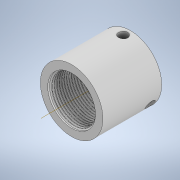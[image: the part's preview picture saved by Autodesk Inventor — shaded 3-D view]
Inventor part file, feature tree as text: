
AUTODESK INVENTOR PART (.ipt)
format: ipt  version: 2021.1 (Build 251245000, 245)  size: 671,232 bytes
history: native  units: in
note: dims shown in document units (in); Inventor stores cm internally (conversion verified against a paired STEP export)
features: sketch x4, extrude x2, helix x1, plane x1, hole x1, pattern_circular x1
ambient origin geometry x8: Origin, YZ Plane, XZ Plane, XY Plane, X Axis, Y Axis, Z Axis, Center Point
bodies: Body1 (feature_tree)
feature tree (10):
  extrude  "Extrusion3"  Depth=2.125in
  extrude  "Extrusion4"  Depth=1.6232in
  helix  "Coil2"  [1 undecoded]
  plane  "Work Plane1"
  hole  "Hole1"  [1 undecoded]
  pattern_circular  "Circular Pattern1"  [2 undecoded]
  sketch  "Sketch3"  dims[d8=0.635in d9=2.125in]
  sketch  "Sketch4"  dims[d10=2.0in d11=0.0in d12=1.6232in d13=1.5in]
  sketch  "Sketch5"  dims[d14=0.0in d15=60.0deg]
  sketch  "Sketch6"  dims[d17=0.0088in d18=0.762in d27=0.0in d28=0.0833in d29=1.5in d30=0.3937in d31=0.0in d32=90.0deg d33=90.0deg d34=0.0in d35=0.0in d36=1.0625in d37=0.25in d38=0.266in d39=2.0in d40=0.316in d41=0.289in d42=0.5635in d43=2.625in d44=0.0in d45=1.1811in d46=360.0deg]
note: 4 required parameter values undecoded (feature->parameter linkage not recoverable at this tier; creation-order binding heuristic only, values carry confidence <= 0.55)
